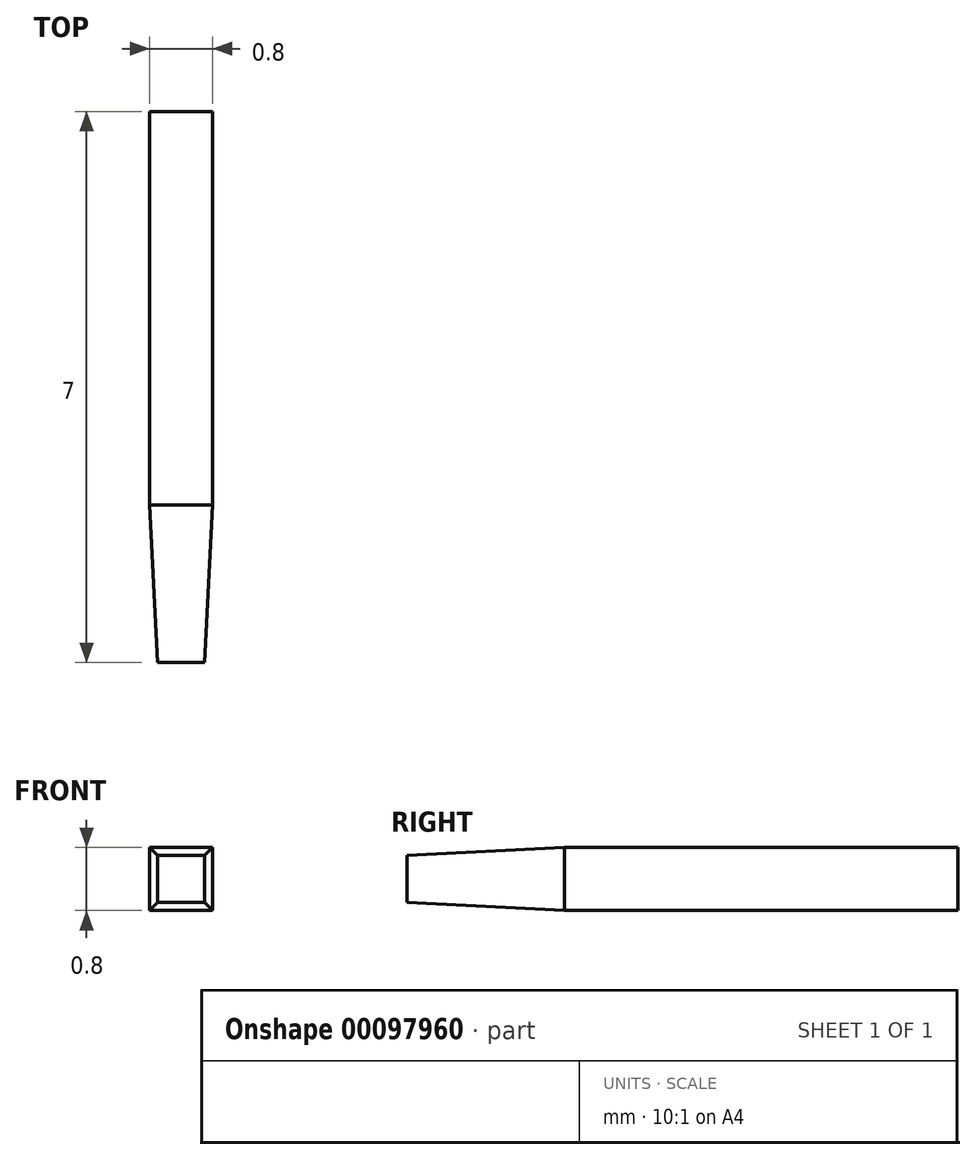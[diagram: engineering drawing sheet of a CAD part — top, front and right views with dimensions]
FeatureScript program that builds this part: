
annotation { "Feature Type Name" : "Feature", "Feature Type Description" : "" }
export const myFeature = defineFeature(function(context is Context, id is Id, definition is map)
    precondition{}
    {
        {
            var Q0;
            Q0=qCreatedBy(makeId("Front.planeOp"),FACE);
            var sketch = newSketch(context, id + "F0", { "sketchPlane" : qUnion([Q0])});
            skLineSegment(sketch, "E0.bottom", {"start": v(-0.4, 0.4) * mm, "end": v(0.4, 0.4) * mm});
            skLineSegment(sketch, "E0.top", {"start": v(-0.4, -0.4) * mm, "end": v(0.4, -0.4) * mm});
            skLineSegment(sketch, "E0.left", {"start": v(-0.4, 0.4) * mm, "end": v(-0.4, -0.4) * mm});
            skLineSegment(sketch, "E0.right", {"start": v(0.4, 0.4) * mm, "end": v(0.4, -0.4) * mm});
            skPoint(sketch, "E0.middle", {"position": v(0, 0) * mm});
            skSolve(sketch);
        }
        {
            var Q0;
            Q0 = qSketchRegion(id + "F0", true);
            extrude(context, id + "F1", {"entities" : qUnion([Q0]), "depth" : 5 * mm});
        }
        {
            var Q0;
            Q0=makeQuery(id+"F1.opExtrude","CAP_FACE",FACE,{"disambiguationData":[OSD([sQuery(id+"F0.wireOp",EDGE,"E0.bottom"),sQuery(id+"F0.wireOp",EDGE,"E0.top"),sQuery(id+"F0.wireOp",EDGE,"E0.left"),sQuery(id+"F0.wireOp",EDGE,"E0.right")])],"isStart":false});
            cPlane(context, id + "F2", {"entities" : qUnion([Q0]), "cplaneType" : CPlaneType.OFFSET, "offset" : 2 * mm, "width" : 150 * mm, "height" : 150 * mm});
        }
        {
            var Q0;
            Q0=qCreatedBy(id+"F2.planeOp",FACE);
            var sketch = newSketch(context, id + "F3", { "sketchPlane" : qUnion([Q0])});
            skLineSegment(sketch, "E1.bottom", {"start": v(0.3, 0.3) * mm, "end": v(-0.3, 0.3) * mm});
            skLineSegment(sketch, "E1.top", {"start": v(0.3, -0.3) * mm, "end": v(-0.3, -0.3) * mm});
            skLineSegment(sketch, "E1.left", {"start": v(0.3, 0.3) * mm, "end": v(0.3, -0.3) * mm});
            skLineSegment(sketch, "E1.right", {"start": v(-0.3, 0.3) * mm, "end": v(-0.3, -0.3) * mm});
            skPoint(sketch, "E1.middle", {"position": v(0, 0) * mm});
            skSolve(sketch);
        }
        {
            var Q1;
            Q1=makeQuery(id+"F1.opExtrude","CAP_FACE",FACE,{"disambiguationData":[OSD([sQuery(id+"F0.wireOp",EDGE,"E0.bottom"),sQuery(id+"F0.wireOp",EDGE,"E0.top"),sQuery(id+"F0.wireOp",EDGE,"E0.left"),sQuery(id+"F0.wireOp",EDGE,"E0.right")])],"isStart":false});
            var Q2;
            Q2=makeQuery(id+"F3.imprint","IMPRINT",FACE,{"disambiguationData":[TD([[makeQuery(id+"F3.imprint","IMPRINT",EDGE,{"derivedFrom":sQuery(id+"F3.wireOp",EDGE,"E1.bottom")}),1.0]])]});
            loft(context, id + "F4", {"operationType" : NewBodyOperationType.ADD, "sheetProfilesArray" : [{ "sheetProfileEntities" : qUnion([Q1]) }, { "sheetProfileEntities" : qUnion([Q2]) }]});
        }
    });
